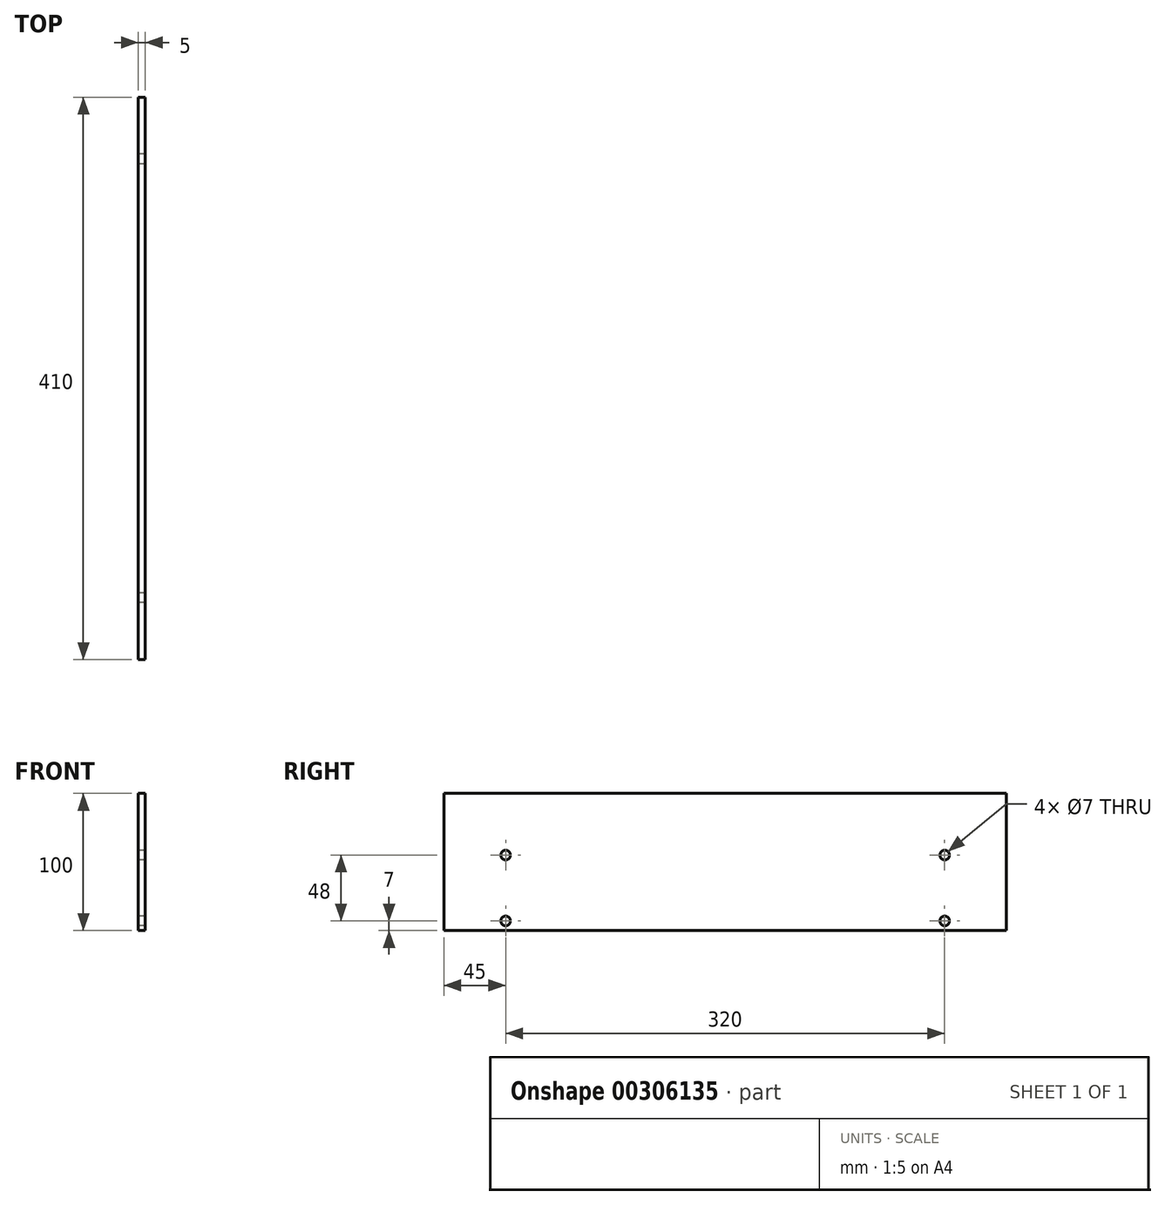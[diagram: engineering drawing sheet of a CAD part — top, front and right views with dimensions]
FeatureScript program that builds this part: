
annotation { "Feature Type Name" : "Feature", "Feature Type Description" : "" }
export const myFeature = defineFeature(function(context is Context, id is Id, definition is map)
    precondition{}
    {
        {
            var Q0;
            Q0=qCreatedBy(makeId("Right.planeOp"),FACE);
            var sketch = newSketch(context, id + "F0", { "sketchPlane" : qUnion([Q0])});
            skLineSegment(sketch, "E0.bottom", {"start": v(-205, 100) * mm, "end": v(205, 100) * mm});
            skLineSegment(sketch, "E0.top", {"start": v(-205, 0) * mm, "end": v(205, 0) * mm});
            skLineSegment(sketch, "E0.left", {"start": v(-205, 100) * mm, "end": v(-205, 0) * mm});
            skLineSegment(sketch, "E0.right", {"start": v(205, 100) * mm, "end": v(205, 0) * mm});
            skPoint(sketch, "E1", {"position": v(-160, 31) * mm});
            skPoint(sketch, "E2", {"position": v(160, 31) * mm});
            skPoint(sketch, "E3", {"position": v(160, 55) * mm});
            skPoint(sketch, "E4", {"position": v(160, 7) * mm});
            skPoint(sketch, "E5", {"position": v(-160, 55) * mm});
            skPoint(sketch, "E6", {"position": v(-160, 7) * mm});
            skCircle(sketch, "E7", {"center": v(-160, 55) * mm, "radius": 3.5 * mm});
            skCircle(sketch, "E8", {"center": v(-160, 7) * mm, "radius": 3.5 * mm});
            skCircle(sketch, "E9", {"center": v(160, 55) * mm, "radius": 3.5 * mm});
            skCircle(sketch, "E10", {"center": v(160, 7) * mm, "radius": 3.5 * mm});
            skSolve(sketch);
        }
        {
            var Q0;
            Q0=makeQuery(id+"F0.imprint","IMPRINT",FACE,{"disambiguationData":[TD([[makeQuery(id+"F0.imprint","IMPRINT",EDGE,{"derivedFrom":sQuery(id+"F0.wireOp",EDGE,"E0.bottom")}),-1.0]])]});
            extrude(context, id + "F1", {"entities" : qUnion([Q0]), "depth" : 5 * mm});
        }
    });
